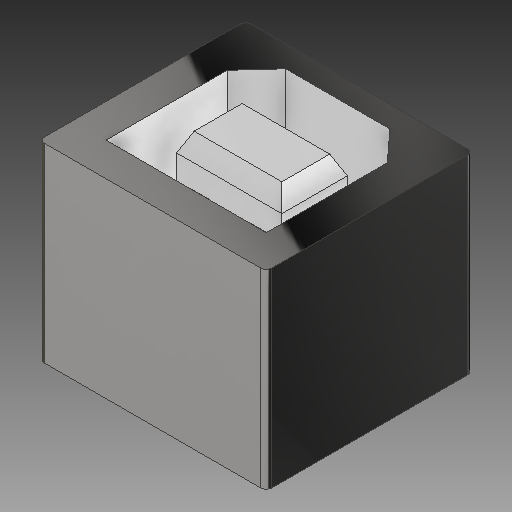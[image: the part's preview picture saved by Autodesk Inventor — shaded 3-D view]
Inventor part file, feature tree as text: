
AUTODESK INVENTOR PART (.ipt)
format: ipt  version: 2019 (Build 230136000, 136)  size: 222,208 bytes
history: native  units: mm
features: sketch x6, extrude x5, fillet x1, projected_geometry x1
ambient origin geometry x8: Origin, YZ Plane, XZ Plane, XY Plane, X Axis, Y Axis, Z Axis, Center Point
bodies: Solid1 (feature_tree)
feature tree (13):
  sketch  "Sketch1"  dims[d0=9.11mm d1=0.0mm d2=1.0mm d3=0.0mm]
  extrude  "Extrusion1"  Depth=1.0mm TaperAngle=0.0deg
  extrude  "Extrusion2"  Depth=1.0mm
  extrude  "Extrusion3"  Depth=0.3mm
  extrude  "Extrusion4"  [1 undecoded]
  extrude  "Extrusion5"  [1 undecoded]
  fillet  "Fillet1"  [1 undecoded]
  sketch  "Sketch2"  dims[d4=8.11mm d5=0.0mm d6=1.0mm d7=-4.363323mm]
  sketch  "Sketch3"  dims[d8=6.84mm d9=0.0mm d10=0.3mm]
  sketch  "Sketch4"
  sketch  "Sketch5"
  projected_geometry  "Projected Loop1"
  sketch  "Sketch6"
note: 3 required parameter values undecoded (feature->parameter linkage not recoverable at this tier; creation-order binding heuristic only, values carry confidence <= 0.55)
